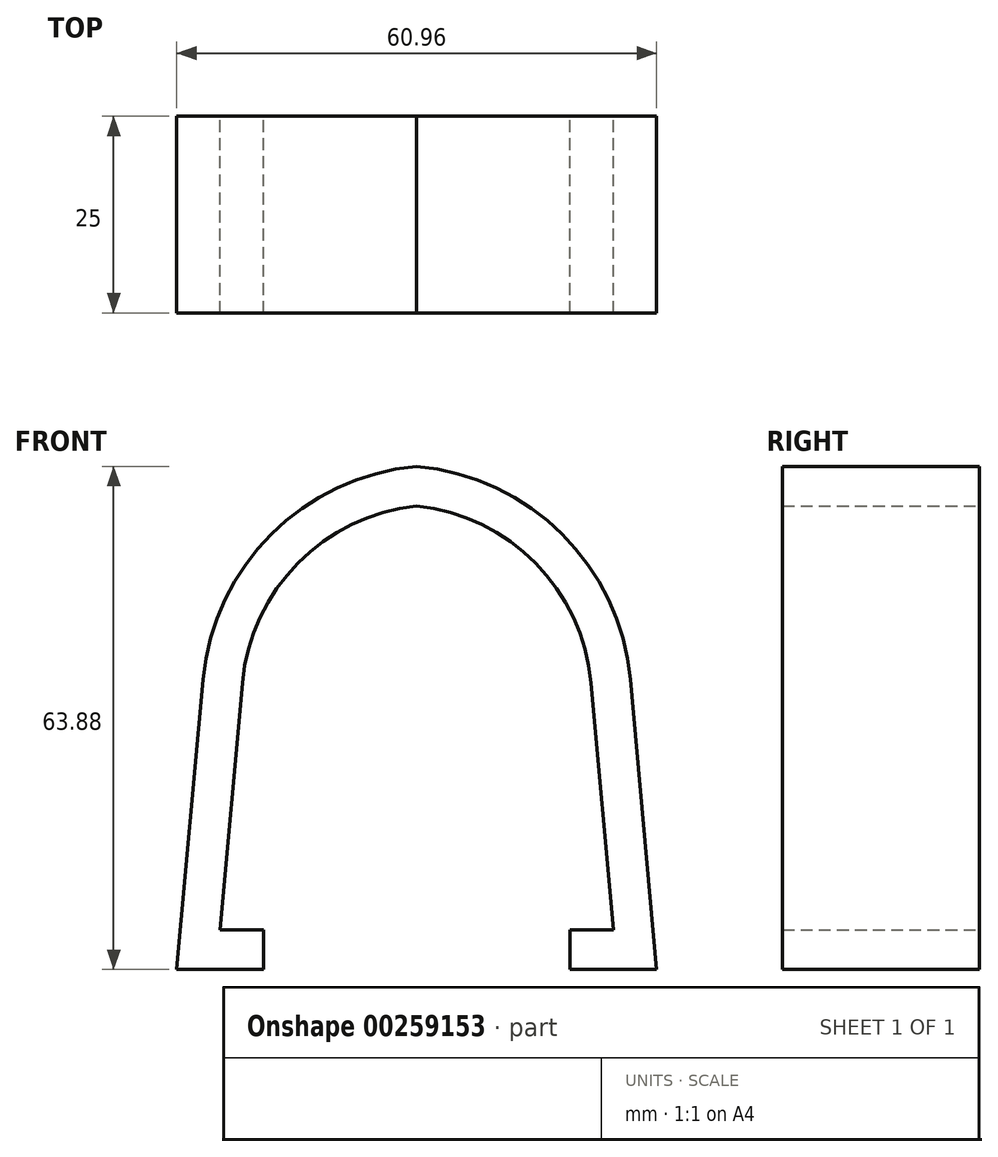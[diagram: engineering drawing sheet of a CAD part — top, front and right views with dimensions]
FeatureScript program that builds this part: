
annotation { "Feature Type Name" : "Feature", "Feature Type Description" : "" }
export const myFeature = defineFeature(function(context is Context, id is Id, definition is map)
    precondition{}
    {
        {
            var Q0;
            Q0=qCreatedBy(makeId("Front.planeOp"),FACE);
            var sketch = newSketch(context, id + "F0", { "sketchPlane" : qUnion([Q0])});
            skLineSegment(sketch, "E0", {"start": v(-22.15, 31.4) * mm, "end": v(-25, 0) * mm});
            skArc(sketch, "E1", {"start": v(0.35, 53.9) * mm, "mid": v(-14.97, 46.72) * mm, "end": v(-22.15, 31.4) * mm});
            skLineSegment(sketch, "E2", {"start": v(-25, 0) * mm, "end": v(-19.48, 0) * mm});
            skLineSegment(sketch, "E3.MirrorCS", {"start": v(22.15, 31.4) * mm, "end": v(25, 0) * mm});
            skLineSegment(sketch, "E4.MirrorCS", {"start": v(25, 0) * mm, "end": v(19.48, 0) * mm});
            skArc(sketch, "E5.MirrorCS", {"start": v(-0.35, 53.9) * mm, "mid": v(14.97, 46.72) * mm, "end": v(22.15, 31.4) * mm});
            skLineSegment(sketch, "E6.0", {"start": v(-30.48, -5) * mm, "end": v(-19.48, -5) * mm});
            skLineSegment(sketch, "E6.1", {"start": v(-27.13, 31.85) * mm, "end": v(-30.48, -5) * mm});
            skLineSegment(sketch, "E6.2", {"start": v(30.48, -5) * mm, "end": v(19.48, -5) * mm});
            skLineSegment(sketch, "E6.3", {"start": v(27.13, 31.85) * mm, "end": v(30.48, -5) * mm});
            skArc(sketch, "E6.4", {"start": v(0, 58.88) * mm, "mid": v(18.47, 50.29) * mm, "end": v(27.13, 31.85) * mm});
            skArc(sketch, "E6.5", {"start": v(0, 58.88) * mm, "mid": v(-18.47, 50.29) * mm, "end": v(-27.13, 31.85) * mm});
            skLineSegment(sketch, "E7", {"start": v(-19.48, 0) * mm, "end": v(-19.48, -5) * mm});
            skLineSegment(sketch, "E8", {"start": v(19.48, 0) * mm, "end": v(19.48, -5) * mm});
            skSolve(sketch);
        }
        {
            var Q0;
            Q0 = qSketchRegion(id + "F0", true);
            extrude(context, id + "F1", {"entities" : qUnion([Q0]), "depth" : 25 * mm});
        }
        {
            var Q0;
            Q0 = qSketchRegion(id + "F0", true);
            extrude(context, id + "F2", {"entities" : qUnion([Q0]), "operationType" : NewBodyOperationType.ADD, "depth" : 15 * mm});
        }
    });
